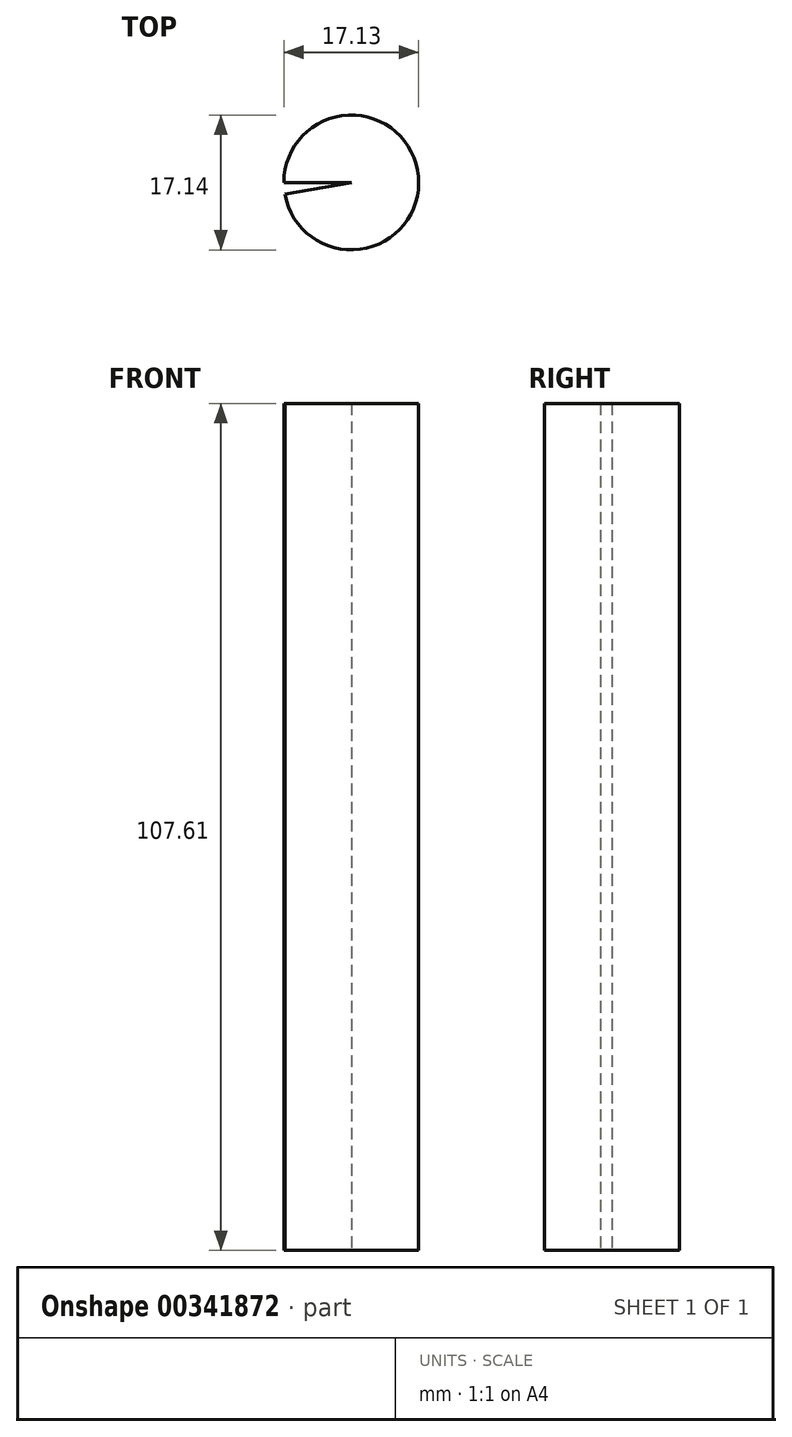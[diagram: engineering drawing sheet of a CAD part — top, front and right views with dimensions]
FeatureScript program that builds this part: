
annotation { "Feature Type Name" : "Feature", "Feature Type Description" : "" }
export const myFeature = defineFeature(function(context is Context, id is Id, definition is map)
    precondition{}
    {
        {
            var Q0;
            Q0=qCreatedBy(makeId("Front.planeOp"),FACE);
            var sketch = newSketch(context, id + "F0", { "sketchPlane" : qUnion([Q0])});
            skLineSegment(sketch, "E0.bottom", {"start": v(-20.61, 54.34) * mm, "end": v(-12.05, 54.34) * mm});
            skLineSegment(sketch, "E0.top", {"start": v(-20.61, -53.27) * mm, "end": v(-12.05, -53.27) * mm});
            skLineSegment(sketch, "E0.left", {"start": v(-20.61, 54.34) * mm, "end": v(-20.61, -53.27) * mm});
            skLineSegment(sketch, "E0.right", {"start": v(-12.05, 54.34) * mm, "end": v(-12.05, -53.27) * mm});
            skLineSegment(sketch, "E1", {"start": v(-12.05, 68.63) * mm, "end": v(-12.05, -53.27) * mm, "construction": true});
            skSolve(sketch);
        }
        {
            var Q0;
            Q0=makeQuery(id+"F0.imprint","IMPRINT",FACE,{"disambiguationData":[TD([[makeQuery(id+"F0.imprint","IMPRINT",EDGE,{"derivedFrom":sQuery(id+"F0.wireOp",EDGE,"E0.bottom")}),-1.0]])]});
            var Q1;
            Q1=sQuery(id+"F0.wireOp",EDGE,"E1");
            revolve(context, id + "F1", {"entities" : qUnion([Q0]), "axis" : qUnion([Q1]), "revolveType" : RevolveType.ONE_DIRECTION, "angle" : 350 * degree});
        }
    });
